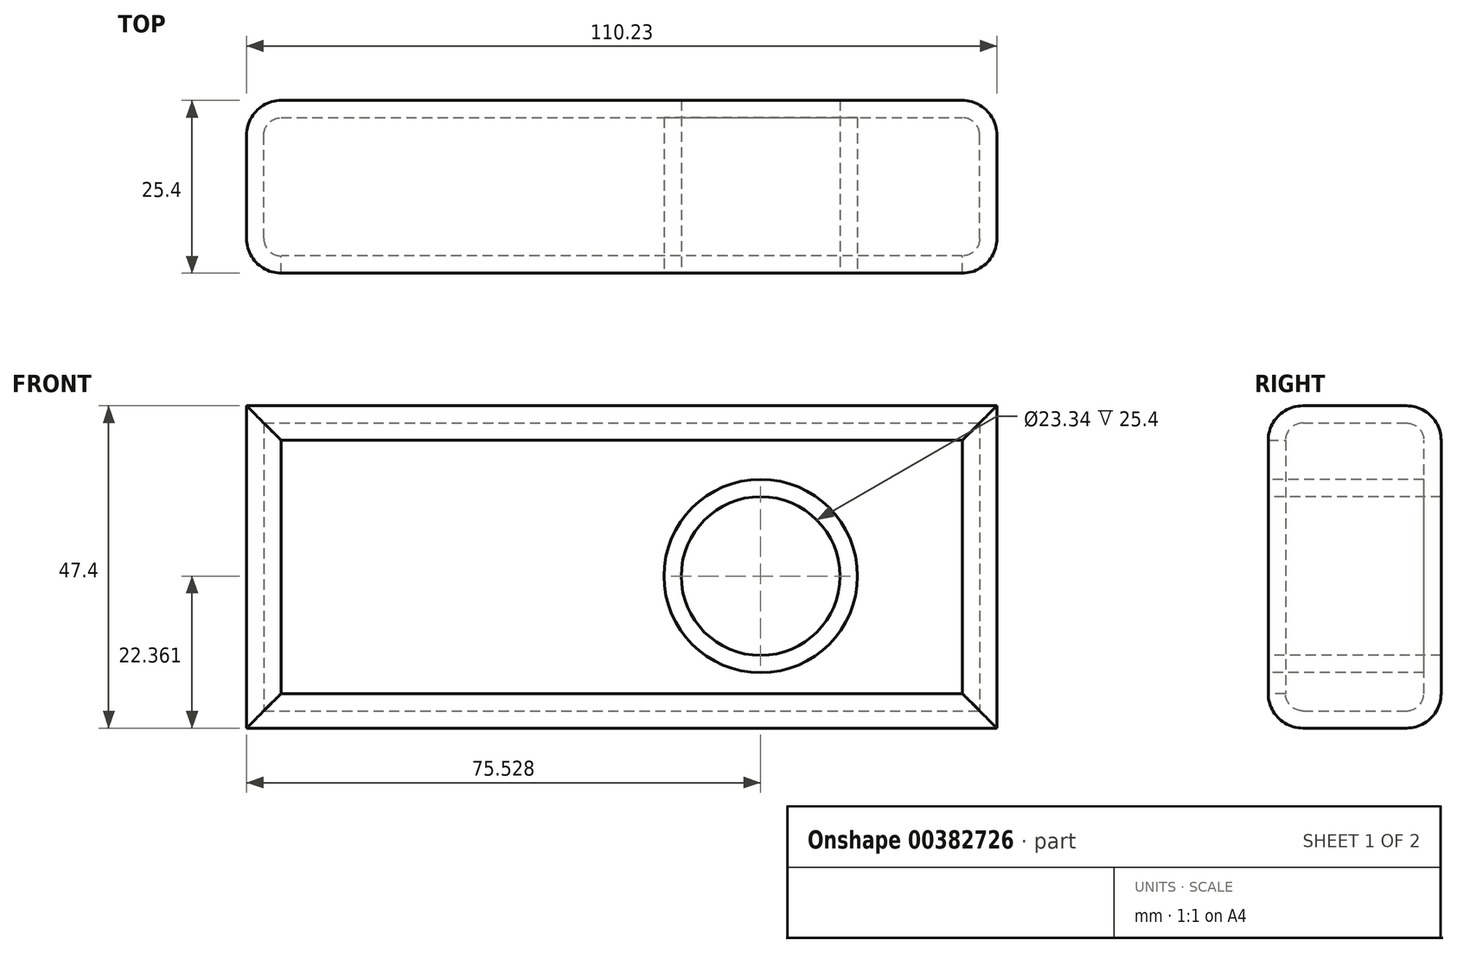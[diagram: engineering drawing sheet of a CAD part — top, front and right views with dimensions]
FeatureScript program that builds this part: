
annotation { "Feature Type Name" : "Feature", "Feature Type Description" : "" }
export const myFeature = defineFeature(function(context is Context, id is Id, definition is map)
    precondition{}
    {
        {
            var Q0;
            Q0=qCreatedBy(makeId("Front.planeOp"),FACE);
            var sketch = newSketch(context, id + "F0", { "sketchPlane" : qUnion([Q0])});
            skLineSegment(sketch, "E0.bottom", {"start": v(-56.07, 14.72) * mm, "end": v(54.16, 14.72) * mm});
            skLineSegment(sketch, "E0.top", {"start": v(-56.07, -32.68) * mm, "end": v(54.16, -32.68) * mm});
            skLineSegment(sketch, "E0.left", {"start": v(-56.07, 14.72) * mm, "end": v(-56.07, -32.68) * mm});
            skLineSegment(sketch, "E0.right", {"start": v(54.16, 14.72) * mm, "end": v(54.16, -32.68) * mm});
            skSolve(sketch);
        }
        {
            var Q0;
            Q0=makeQuery(id+"F0.imprint","IMPRINT",FACE,{"disambiguationData":[TD([[makeQuery(id+"F0.imprint","IMPRINT",EDGE,{"derivedFrom":sQuery(id+"F0.wireOp",EDGE,"E0.bottom")}),-1.0]])]});
            extrude(context, id + "F1", {"entities" : qUnion([Q0]), "depth" : 25.4 * mm});
        }
        {
            var Q0;
            Q0=makeQuery(id+"F1.opExtrude","CAP_FACE",FACE,{"disambiguationData":[OSD([sQuery(id+"F0.wireOp",EDGE,"E0.bottom"),sQuery(id+"F0.wireOp",EDGE,"E0.top"),sQuery(id+"F0.wireOp",EDGE,"E0.left"),sQuery(id+"F0.wireOp",EDGE,"E0.right")])],"isStart":false});
            var sketch = newSketch(context, id + "F2", { "sketchPlane" : qUnion([Q0])});
            skCircle(sketch, "E1", {"center": v(19.46, -10.32) * mm, "radius": 11.67 * mm});
            skSolve(sketch);
        }
        {
            var Q0;
            Q0=makeQuery(id+"F2.imprint","IMPRINT",FACE,{"disambiguationData":[TD([[makeQuery(id+"F2.imprint","IMPRINT",EDGE,{"derivedFrom":sQuery(id+"F2.wireOp",EDGE,"E1")}),1.0]])]});
            extrude(context, id + "F3", {"entities" : qUnion([Q0]), "operationType" : NewBodyOperationType.REMOVE, "endBound" : BoundingType.UP_TO_NEXT, "oppositeDirection" : true, "depth" : 25.4 * mm});
        }
        {
            var Q0;
            Q0=makeQuery(id+"F3.boolean.opBoolean","COPY",EDGE,{"derivedFrom":makeQuery(id+"F3.opExtrude","CAP_EDGE",EDGE,{"disambiguationData":[OSD([sQuery(id+"F2.wireOp",EDGE,"E1")])],"isStart":true})});
            var Q1;
            Q1=makeQuery(id+"F1.opExtrude","CAP_EDGE",EDGE,{"disambiguationData":[OSD([sQuery(id+"F0.wireOp",EDGE,"E0.bottom")])],"isStart":false});
            var Q2;
            Q2=makeQuery(id+"F1.opExtrude","CAP_EDGE",EDGE,{"disambiguationData":[OSD([sQuery(id+"F0.wireOp",EDGE,"E0.right")])],"isStart":false});
            var Q3;
            Q3=makeQuery(id+"F1.opExtrude","CAP_EDGE",EDGE,{"disambiguationData":[OSD([sQuery(id+"F0.wireOp",EDGE,"E0.top")])],"isStart":false});
            var Q4;
            Q4=makeQuery(id+"F1.opExtrude","CAP_EDGE",EDGE,{"disambiguationData":[OSD([sQuery(id+"F0.wireOp",EDGE,"E0.left")])],"isStart":false});
            var Q5;
            Q5=makeQuery(id+"F3.boolean.opBoolean","COPY",EDGE,{"derivedFrom":makeQuery(id+"F3.opExtrude","CAP_EDGE",EDGE,{"disambiguationData":[OSD([sQuery(id+"F2.wireOp",EDGE,"E1")])],"isStart":false})});
            fillet(context, id + "F4", {"entities" : qUnion([Q0, Q1, Q2, Q3, Q4, Q5]), "radius" : 5.08 * mm, "tangentPropagation" : true, "allowEdgeOverflow" : false});
        }
        {
            var Q0;
            Q0=makeQuery(id+"F1.opExtrude","CAP_EDGE",EDGE,{"disambiguationData":[OSD([sQuery(id+"F0.wireOp",EDGE,"E0.bottom")])],"isStart":true});
            var Q1;
            Q1=makeQuery(id+"F1.opExtrude","CAP_EDGE",EDGE,{"disambiguationData":[OSD([sQuery(id+"F0.wireOp",EDGE,"E0.left")])],"isStart":true});
            var Q2;
            Q2=makeQuery(id+"F1.opExtrude","CAP_EDGE",EDGE,{"disambiguationData":[OSD([sQuery(id+"F0.wireOp",EDGE,"E0.top")])],"isStart":true});
            var Q3;
            Q3=makeQuery(id+"F1.opExtrude","CAP_EDGE",EDGE,{"disambiguationData":[OSD([sQuery(id+"F0.wireOp",EDGE,"E0.right")])],"isStart":true});
            fillet(context, id + "F5", {"entities" : qUnion([Q0, Q1, Q2, Q3]), "radius" : 5.08 * mm, "tangentPropagation" : true, "allowEdgeOverflow" : false});
        }
        {
            var Q0;
            Q0=makeQuery(id+"F1.opExtrude","CAP_FACE",FACE,{"disambiguationData":[OSD([sQuery(id+"F0.wireOp",EDGE,"E0.bottom"),sQuery(id+"F0.wireOp",EDGE,"E0.top"),sQuery(id+"F0.wireOp",EDGE,"E0.left"),sQuery(id+"F0.wireOp",EDGE,"E0.right")])],"isStart":false});
            shell(context, id + "F6", {"entities" : qUnion([Q0]), "thickness" : 2.54 * mm});
        }
    });
